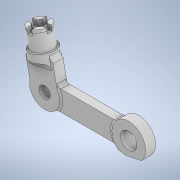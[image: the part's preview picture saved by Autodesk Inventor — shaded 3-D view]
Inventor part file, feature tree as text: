
AUTODESK INVENTOR PART (.ipt)
format: ipt  version: 2022.6 (Build 266554000, 554)  size: 367,104 bytes
history: native  units: mm
features: sketch x11, extrude x10, projected_geometry x5, fillet x2, revolve x1
ambient origin geometry x8: Origin, YZ Plane, XZ Plane, XY Plane, X Axis, Y Axis, Z Axis, Center Point
bodies: Solid1 (feature_tree)
feature tree (29):
  extrude  "Extrusion1"  Depth=3.0mm TaperAngle=0.0deg
  extrude  "Extrusion2"  Depth=2.0mm
  revolve  "Revolution1"  [1 undecoded]
  extrude  "Extrusion3"  Depth=7.8mm
  extrude  "Extrusion4"  Depth=17.715092mm
  extrude  "Extrusion5"  TaperAngle=90.0deg  [1 undecoded]
  fillet  "Fillet2"  [1 undecoded]
  extrude  "Extrusion7"  Depth=2.828mm
  extrude  "Extrusion8"  Depth=10.0mm
  extrude  "Extrusion10"  Depth=10.0mm
  extrude  "Extrusion11"  Depth=6.0mm TaperAngle=0.0deg
  fillet  "Fillet5"  Radius=3.4mm
  extrude  "Extrusion12"  Depth=2.0mm
  sketch  "Sketch1"  dims[d2=25.0mm d3=3.0mm d4=0.0mm]
  sketch  "Sketch2"  dims[d5=2.0mm d7=3.0mm]
  projected_geometry  "Projected Loop1"
  sketch  "Sketch3"  dims[d8=2.5mm d9=0.0mm d13=8.0mm]
  sketch  "Sketch4"  dims[d14=1.5mm d15=7.8mm]
  projected_geometry  "Projected Loop2"
  sketch  "Sketch5"  dims[d16=3.0mm d17=17.715092mm]
  sketch  "Sketch6"  dims[d18=6.834775mm d19=90.0deg d21=0.0mm d22=0.0mm]
  sketch  "Sketch8"  dims[d23=3.0mm d24=2.828mm]
  projected_geometry  "Projected Loop3"
  sketch  "Sketch9"  dims[d25=10.0mm d26=0.0mm d27=4.9mm]
  projected_geometry  "Projected Loop4"
  sketch  "Sketch11"  dims[d28=10.0mm d30=5.687mm]
  sketch  "Sketch12"  dims[d31=6.1mm d32=6.0mm d33=0.0mm d35=3.4mm]
  sketch  "Sketch13"  dims[d36=9.0mm d37=1.0mm d45=1.396263mm d46=5.0mm d47=0.0mm d48=0.0mm d49=6.0mm d50=27.925268mm d52=0.0mm d58=1.5mm d59=0.0mm d64=6.0mm d65=6.1mm d66=7.0mm d67=0.0mm d68=7.2mm d69=6.0mm d70=2.2mm d71=0.0mm d72=2.0mm d73=5.8mm d74=0.4mm d75=0.0mm d76=1.5mm d77=40.0mm d79=360.0deg d81=3.5mm d20=0.872665mm d29=0.5mm]
  projected_geometry  "Projected Loop8"
note: 3 required parameter values undecoded (feature->parameter linkage not recoverable at this tier; creation-order binding heuristic only, values carry confidence <= 0.55)